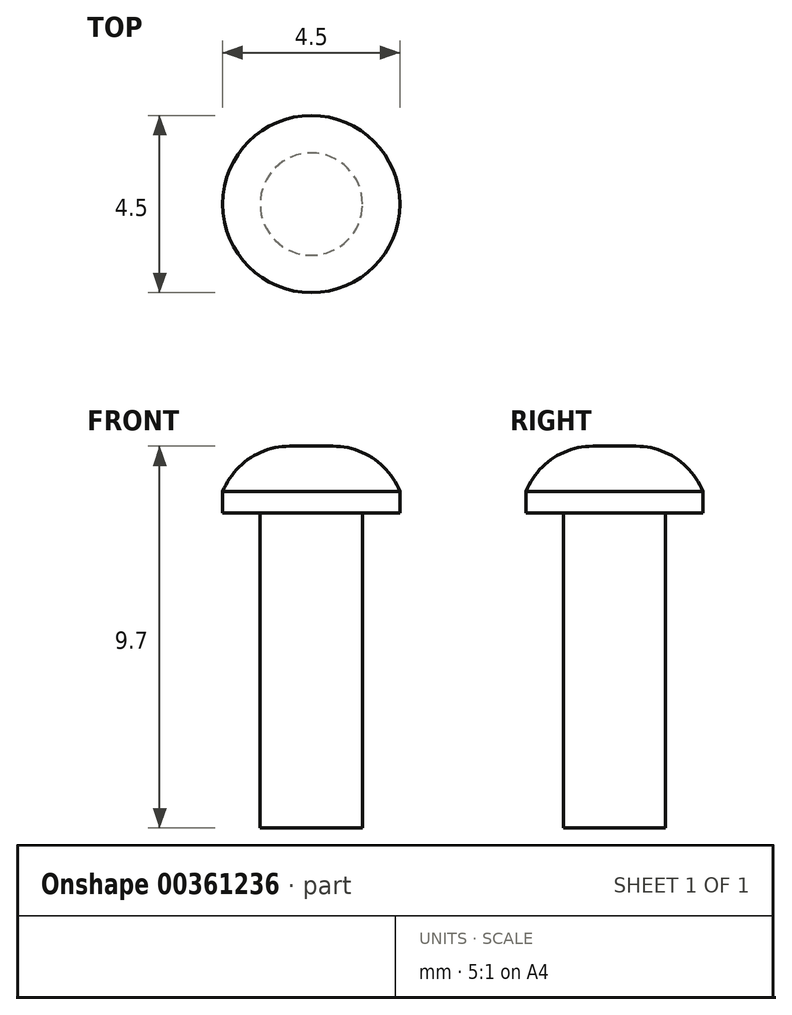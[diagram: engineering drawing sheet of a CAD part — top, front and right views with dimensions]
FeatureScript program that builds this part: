
annotation { "Feature Type Name" : "Feature", "Feature Type Description" : "" }
export const myFeature = defineFeature(function(context is Context, id is Id, definition is map)
    precondition{}
    {
        {
            var Q0;
            Q0=qCreatedBy(makeId("Front.planeOp"),FACE);
            var sketch = newSketch(context, id + "F0", { "sketchPlane" : qUnion([Q0])});
            skLineSegment(sketch, "E0", {"start": v(0, 0) * mm, "end": v(0, 1.7) * mm});
            skLineSegment(sketch, "E1", {"start": v(0, 0) * mm, "end": v(2.25, 0) * mm});
            skLineSegment(sketch, "E2", {"start": v(2.25, 0) * mm, "end": v(2.25, 0.55) * mm});
            skLineSegment(sketch, "E3", {"start": v(0, 1.7) * mm, "end": v(0.55, 1.7) * mm});
            skArc(sketch, "E4", {"start": v(2.25, 0.55) * mm, "mid": v(1.58, 1.38) * mm, "end": v(0.55, 1.7) * mm});
            skSolve(sketch);
        }
        {
            var Q0;
            Q0=qSketchRegion(id+"F0",true);
            var Q1;
            Q1=sQuery(id+"F0.wireOp",EDGE,"E0");
            revolve(context, id + "F1", {"surfaceOperationType" : NewSurfaceOperationType.NEW, "entities" : qUnion([Q0]), "axis" : qUnion([Q1]), "revolveType" : RevolveType.FULL});
        }
        {
            var Q0;
            Q0=makeQuery(id+"F1.opRevolve","SWEPT_BODY",BODY,{"disambiguationData":[OSD([sQuery(id+"F0.wireOp",EDGE,"E0"),sQuery(id+"F0.wireOp",EDGE,"E1"),sQuery(id+"F0.wireOp",EDGE,"E2"),sQuery(id+"F0.wireOp",EDGE,"E3"),sQuery(id+"F0.wireOp",EDGE,"E4")])]});
            transform(context, id + "F2", {"entities" : qUnion([Q0]), "transformType" : TransformType.TRANSLATION_3D, "dx" : 0 * mm, "dy" : 0 * mm, "dz" : 0 * mm, "makeCopy" : true});
        }
        {
            var Q0;
            Q0=makeQuery(id+"F1.opRevolve","SWEPT_BODY",BODY,{"disambiguationData":[OSD([sQuery(id+"F0.wireOp",EDGE,"E0"),sQuery(id+"F0.wireOp",EDGE,"E1"),sQuery(id+"F0.wireOp",EDGE,"E2"),sQuery(id+"F0.wireOp",EDGE,"E3"),sQuery(id+"F0.wireOp",EDGE,"E4")])]});
            transform(context, id + "F3", {"entities" : qUnion([Q0]), "transformType" : TransformType.COPY});
        }
        {
            var Q0;
            Q0=makeQuery(id+"F1.opRevolve","SWEPT_BODY",BODY,{"disambiguationData":[OSD([sQuery(id+"F0.wireOp",EDGE,"E0"),sQuery(id+"F0.wireOp",EDGE,"E1"),sQuery(id+"F0.wireOp",EDGE,"E2"),sQuery(id+"F0.wireOp",EDGE,"E3"),sQuery(id+"F0.wireOp",EDGE,"E4")])]});
            transform(context, id + "F4", {"entities" : qUnion([Q0]), "transformType" : TransformType.COPY});
        }
        {
            var Q0;
            Q0=makeQuery(id+"F1.opRevolve","SWEPT_FACE",FACE,{"disambiguationData":[OSD([sQuery(id+"F0.wireOp",EDGE,"E1")])]});
            var sketch = newSketch(context, id + "F5", { "sketchPlane" : qUnion([Q0])});
            skCircle(sketch, "E5", {"center": v(0, 0) * mm, "radius": 1.3 * mm});
            skSolve(sketch);
        }
        {
            var Q0;
            Q0=qSketchRegion(id+"F5",true);
            extrude(context, id + "F6", {"entities" : qUnion([Q0]), "operationType" : NewBodyOperationType.ADD, "depth" : 6 * mm, "offsetDistance" : 25 * mm});
        }
        {
            var Q0;
            Q0=qSketchRegion(id+"F5",true);
            extrude(context, id + "F7", {"entities" : qUnion([Q0]), "operationType" : NewBodyOperationType.ADD, "depth" : 8 * mm, "offsetDistance" : 25 * mm});
        }
        {
            var Q0;
            Q0=qSketchRegion(id+"F5",true);
            extrude(context, id + "F8", {"entities" : qUnion([Q0]), "operationType" : NewBodyOperationType.ADD, "depth" : 5 * mm, "offsetDistance" : 25 * mm});
        }
        {
            var Q0;
            Q0=qCreatedBy(makeId("Front.planeOp"),FACE);
            var sketch = newSketch(context, id + "F9", { "sketchPlane" : qUnion([Q0])});
            skLineSegment(sketch, "E6", {"start": v(0, 1.3) * mm, "end": v(0, 0) * mm});
            skLineSegment(sketch, "E7", {"start": v(0, 0) * mm, "end": v(1.75, 0) * mm});
            skLineSegment(sketch, "E8", {"start": v(1.75, 0) * mm, "end": v(1.75, 0.33) * mm});
            skLineSegment(sketch, "E9", {"start": v(0, 1.3) * mm, "end": v(0.43, 1.3) * mm});
            skArc(sketch, "E10", {"start": v(1.75, 0.33) * mm, "mid": v(1.25, 1.03) * mm, "end": v(0.43, 1.3) * mm});
            skSolve(sketch);
        }
        {
            var Q0;
            Q0=qSketchRegion(id+"F9",true);
            var Q1;
            Q1=sQuery(id+"F9.wireOp",EDGE,"E6");
            revolve(context, id + "F10", {"surfaceOperationType" : NewSurfaceOperationType.NEW, "entities" : qUnion([Q0]), "axis" : qUnion([Q1]), "revolveType" : RevolveType.FULL});
        }
        {
            var Q0;
            Q0=makeQuery(id+"F10.opRevolve","SWEPT_FACE",FACE,{"disambiguationData":[OSD([sQuery(id+"F9.wireOp",EDGE,"E7")])]});
            var sketch = newSketch(context, id + "F11", { "sketchPlane" : qUnion([Q0])});
            skCircle(sketch, "E11", {"center": v(0, 0) * mm, "radius": 1 * mm});
            skSolve(sketch);
        }
        {
            var Q0;
            Q0=qSketchRegion(id+"F11",true);
            extrude(context, id + "F12", {"entities" : qUnion([Q0]), "operationType" : NewBodyOperationType.ADD, "depth" : 6 * mm, "offsetDistance" : 25 * mm});
        }
        {
            var Q0;
            Q0=qSketchRegion(id+"F5",true);
            extrude(context, id + "F13", {"entities" : qUnion([Q0]), "operationType" : NewBodyOperationType.ADD, "depth" : 5 * mm, "offsetDistance" : 25 * mm});
        }
    });
